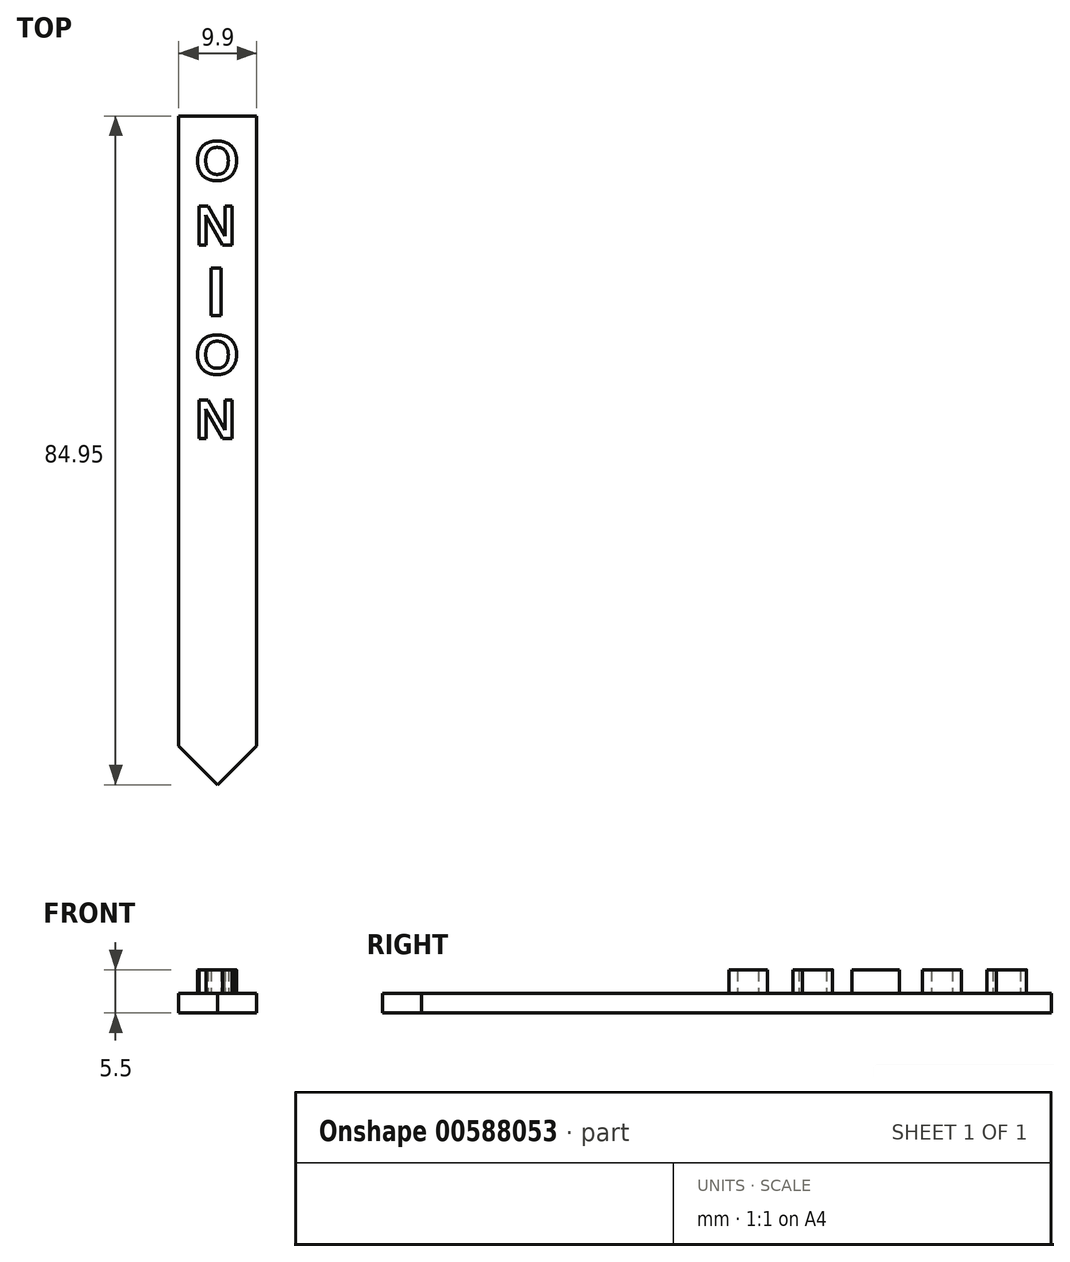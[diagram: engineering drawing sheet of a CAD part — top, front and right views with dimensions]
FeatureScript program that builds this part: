
annotation { "Feature Type Name" : "Feature", "Feature Type Description" : "" }
export const myFeature = defineFeature(function(context is Context, id is Id, definition is map)
    precondition{}
    {
        {
            var Q0;
            Q0=qCreatedBy(makeId("Top.planeOp"),FACE);
            var sketch = newSketch(context, id + "F0", { "sketchPlane" : qUnion([Q0])});
            skLineSegment(sketch, "E0", {"start": v(0, 0) * mm, "end": v(4.95, 4.95) * mm});
            skLineSegment(sketch, "E1", {"start": v(0, 0) * mm, "end": v(-4.95, 4.95) * mm});
            skPoint(sketch, "E2.end.orphan", {"position": v(-3.53, 0) * mm});
            skPoint(sketch, "E3.end.orphan", {"position": v(4.95, 0) * mm});
            skLineSegment(sketch, "E4", {"start": v(4.95, 4.95) * mm, "end": v(4.95, 84.95) * mm});
            skLineSegment(sketch, "E5", {"start": v(-4.95, 4.95) * mm, "end": v(-4.95, 84.95) * mm});
            skLineSegment(sketch, "E6", {"start": v(-4.95, 84.95) * mm, "end": v(4.95, 84.95) * mm});
            skSolve(sketch);
        }
        {
            var Q0;
            Q0=qSketchRegion(id+"F0",true);
            extrude(context, id + "F1", {"entities" : qUnion([Q0]), "depth" : 2.5 * mm, "offsetDistance" : 25 * mm});
        }
        {
            var Q0;
            Q0=makeQuery(id+"F1.opExtrude","CAP_FACE",FACE,{"disambiguationData":[OSD([sQuery(id+"F0.wireOp",EDGE,"E0"),sQuery(id+"F0.wireOp",EDGE,"E1"),sQuery(id+"F0.wireOp",EDGE,"E4"),sQuery(id+"F0.wireOp",EDGE,"E5"),sQuery(id+"F0.wireOp",EDGE,"E6")])],"isStart":false});
            var sketch = newSketch(context, id + "F2", { "sketchPlane" : qUnion([Q0])});
            skText(sketch, "E7", { "text": "O\nN\n \nO\nN", "fontName": "Arimo-Bold.ttf"});
            skText(sketch, "E8", { "text": "I", "fontName": "OpenSans-Bold.ttf"});
            const initialGuessF2  = {"E7": [-0.00286, 0.0768, 1, 0, 0.00514], "E8": [-0.00163, 0.0596, 1, 0, 0.00607]};
            skSetInitialGuess(sketch, initialGuessF2);
            skSolve(sketch);
        }
        {
            var Q0;
            Q0 = qSketchRegion(id + "F2", true);
            extrude(context, id + "F3", {"entities" : qUnion([Q0]), "operationType" : NewBodyOperationType.ADD, "depth" : 3 * mm, "offsetDistance" : 25 * mm});
        }
    });
